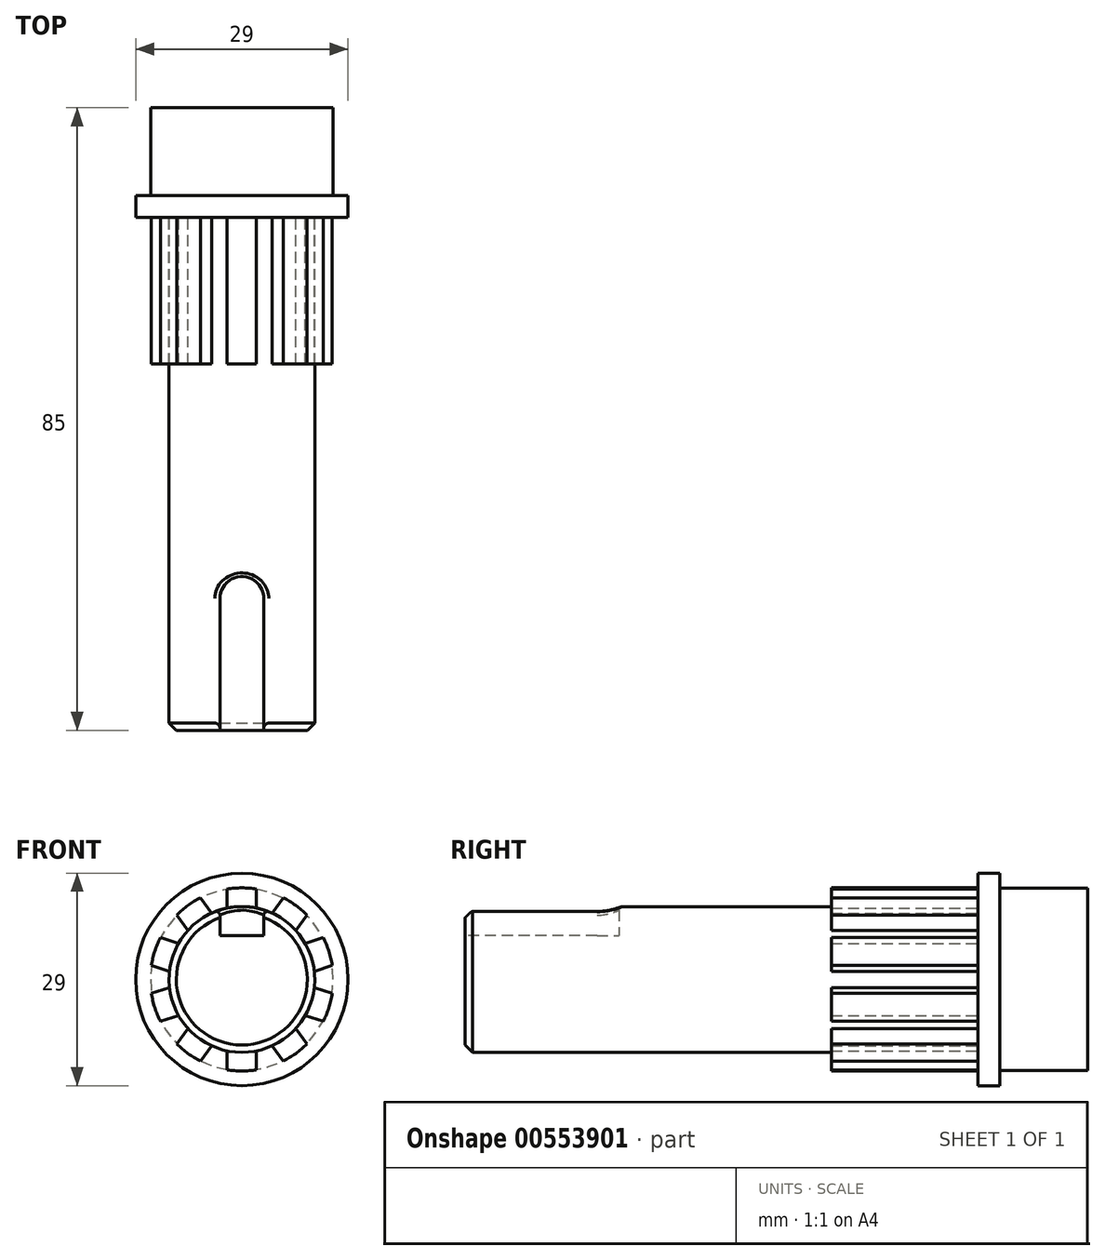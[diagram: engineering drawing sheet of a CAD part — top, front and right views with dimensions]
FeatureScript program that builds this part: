
annotation { "Feature Type Name" : "Feature", "Feature Type Description" : "" }
export const myFeature = defineFeature(function(context is Context, id is Id, definition is map)
    precondition{}
    {
        {
            var Q0;
            Q0=qCreatedBy(makeId("Front.planeOp"),FACE);
            var sketch = newSketch(context, id + "F0", { "sketchPlane" : qUnion([Q0])});
            skCircle(sketch, "E0", {"center": v(0, 0) * mm, "radius": 12.45 * mm});
            skSolve(sketch);
        }
        {
            var Q0;
            Q0=makeQuery(id+"F0.imprint","IMPRINT",FACE,{"disambiguationData":[TD([[makeQuery(id+"F0.imprint","IMPRINT",EDGE,{"derivedFrom":sQuery(id+"F0.wireOp",EDGE,"E0")}),1.0]])]});
            extrude(context, id + "F1", {"entities" : qUnion([Q0]), "oppositeDirection" : true, "depth" : 12 * mm, "offsetDistance" : 25 * mm});
        }
        {
            var Q0;
            Q0=qCreatedBy(makeId("Front.planeOp"),FACE);
            var sketch = newSketch(context, id + "F2", { "sketchPlane" : qUnion([Q0])});
            skCircle(sketch, "E1", {"center": v(0, 0) * mm, "radius": 14.5 * mm});
            skSolve(sketch);
        }
        {
            var Q0;
            Q0=makeQuery(id+"F2.imprint","IMPRINT",FACE,{"disambiguationData":[TD([[makeQuery(id+"F2.imprint","IMPRINT",EDGE,{"derivedFrom":sQuery(id+"F2.wireOp",EDGE,"E1")}),1.0]])]});
            extrude(context, id + "F3", {"entities" : qUnion([Q0]), "operationType" : NewBodyOperationType.ADD, "depth" : 3 * mm, "offsetDistance" : 25 * mm});
        }
        {
            var Q0;
            Q0=makeQuery(id+"F3.opExtrude","CAP_FACE",FACE,{"disambiguationData":[OSD([sQuery(id+"F2.wireOp",EDGE,"E1")])],"isStart":false});
            var sketch = newSketch(context, id + "F4", { "sketchPlane" : qUnion([Q0])});
            skCircle(sketch, "E2", {"center": v(0, 0) * mm, "radius": 9.95 * mm});
            skSolve(sketch);
        }
        {
            var Q0;
            Q0=makeQuery(id+"F4.imprint","IMPRINT",FACE,{"disambiguationData":[TD([[makeQuery(id+"F4.imprint","IMPRINT",EDGE,{"derivedFrom":sQuery(id+"F4.wireOp",EDGE,"E2")}),1.0]])]});
            extrude(context, id + "F5", {"entities" : qUnion([Q0]), "operationType" : NewBodyOperationType.ADD, "depth" : 70 * mm, "offsetDistance" : 25 * mm});
        }
        {
            var Q0;
            Q0=makeQuery(id+"F3.opExtrude","CAP_FACE",FACE,{"disambiguationData":[OSD([sQuery(id+"F2.wireOp",EDGE,"E1")])],"isStart":false});
            var sketch = newSketch(context, id + "F6", { "sketchPlane" : qUnion([Q0])});
            skArc(sketch, "E3", {"start": v(2, 12.34) * mm, "mid": v(0, 12.5) * mm, "end": v(-2, 12.34) * mm});
            skLineSegment(sketch, "E4", {"start": v(-2, 12.34) * mm, "end": v(-2, 8.4) * mm});
            skLineSegment(sketch, "E5", {"start": v(2, 8.4) * mm, "end": v(2, 12.34) * mm});
            skPoint(sketch, "E6.end.orphan", {"position": v(0.2, 8.4) * mm});
            skLineSegment(sketch, "E7.1.0", {"start": v(-8.87, 8.8) * mm, "end": v(-6.56, 5.63) * mm});
            skArc(sketch, "E7.1.1", {"start": v(-5.63, 11.16) * mm, "mid": v(-7.35, 10.11) * mm, "end": v(-8.87, 8.8) * mm});
            skLineSegment(sketch, "E7.1.2", {"start": v(-3.32, 7.98) * mm, "end": v(-5.63, 11.16) * mm});
            skLineSegment(sketch, "E7.2.0", {"start": v(-12.35, 1.91) * mm, "end": v(-8.62, 0.7) * mm});
            skArc(sketch, "E7.2.1", {"start": v(-11.12, 5.72) * mm, "mid": v(-11.89, 3.86) * mm, "end": v(-12.35, 1.91) * mm});
            skLineSegment(sketch, "E7.2.2", {"start": v(-7.38, 4.5) * mm, "end": v(-11.12, 5.72) * mm});
            skLineSegment(sketch, "E7.3.0", {"start": v(-11.12, -5.72) * mm, "end": v(-7.38, -4.5) * mm});
            skArc(sketch, "E7.3.1", {"start": v(-12.35, -1.91) * mm, "mid": v(-11.89, -3.86) * mm, "end": v(-11.12, -5.72) * mm});
            skLineSegment(sketch, "E7.3.2", {"start": v(-8.62, -0.7) * mm, "end": v(-12.35, -1.91) * mm});
            skLineSegment(sketch, "E7.4.0", {"start": v(-5.63, -11.16) * mm, "end": v(-3.32, -7.98) * mm});
            skArc(sketch, "E7.4.1", {"start": v(-8.87, -8.8) * mm, "mid": v(-7.35, -10.11) * mm, "end": v(-5.63, -11.16) * mm});
            skLineSegment(sketch, "E7.4.2", {"start": v(-6.56, -5.63) * mm, "end": v(-8.87, -8.8) * mm});
            skLineSegment(sketch, "E7.5.0", {"start": v(2, -12.34) * mm, "end": v(2, -8.4) * mm});
            skArc(sketch, "E7.5.1", {"start": v(-2, -12.34) * mm, "mid": v(0, -12.5) * mm, "end": v(2, -12.34) * mm});
            skLineSegment(sketch, "E7.5.2", {"start": v(-2, -8.4) * mm, "end": v(-2, -12.34) * mm});
            skLineSegment(sketch, "E7.6.0", {"start": v(8.87, -8.8) * mm, "end": v(6.56, -5.63) * mm});
            skArc(sketch, "E7.6.1", {"start": v(5.63, -11.16) * mm, "mid": v(7.35, -10.11) * mm, "end": v(8.87, -8.8) * mm});
            skLineSegment(sketch, "E7.6.2", {"start": v(3.32, -7.98) * mm, "end": v(5.63, -11.16) * mm});
            skLineSegment(sketch, "E7.7.0", {"start": v(12.35, -1.91) * mm, "end": v(8.62, -0.7) * mm});
            skArc(sketch, "E7.7.1", {"start": v(11.12, -5.72) * mm, "mid": v(11.89, -3.86) * mm, "end": v(12.35, -1.91) * mm});
            skLineSegment(sketch, "E7.7.2", {"start": v(7.38, -4.5) * mm, "end": v(11.12, -5.72) * mm});
            skLineSegment(sketch, "E7.8.0", {"start": v(11.12, 5.72) * mm, "end": v(7.38, 4.5) * mm});
            skArc(sketch, "E7.8.1", {"start": v(12.35, 1.91) * mm, "mid": v(11.89, 3.86) * mm, "end": v(11.12, 5.72) * mm});
            skLineSegment(sketch, "E7.8.2", {"start": v(8.62, 0.7) * mm, "end": v(12.35, 1.91) * mm});
            skLineSegment(sketch, "E7.9.0", {"start": v(5.63, 11.16) * mm, "end": v(3.32, 7.98) * mm});
            skArc(sketch, "E7.9.1", {"start": v(8.87, 8.8) * mm, "mid": v(7.35, 10.11) * mm, "end": v(5.63, 11.16) * mm});
            skLineSegment(sketch, "E7.9.2", {"start": v(6.56, 5.63) * mm, "end": v(8.87, 8.8) * mm});
            skSolve(sketch);
        }
        {
            var Q0;
            {var subQ0=sQuery(id+"F6.wireOp",EDGE,"E3");Q0=makeQuery(id+"F6.imprint","IMPRINT",FACE,{"disambiguationData":[TD([[makeQuery(id+"F6.imprint","IMPRINT",EDGE,{"derivedFrom":subQ0}),1.0]])]});}
            var Q1;
            {var subQ0=sQuery(id+"F6.wireOp",EDGE,"E7.1.1");Q1=makeQuery(id+"F6.imprint","IMPRINT",FACE,{"disambiguationData":[TD([[makeQuery(id+"F6.imprint","IMPRINT",EDGE,{"derivedFrom":subQ0}),1.0]])]});}
            var Q2;
            {var subQ0=sQuery(id+"F6.wireOp",EDGE,"E7.2.1");Q2=makeQuery(id+"F6.imprint","IMPRINT",FACE,{"disambiguationData":[TD([[makeQuery(id+"F6.imprint","IMPRINT",EDGE,{"derivedFrom":subQ0}),1.0]])]});}
            var Q3;
            {var subQ0=sQuery(id+"F6.wireOp",EDGE,"E7.3.1");Q3=makeQuery(id+"F6.imprint","IMPRINT",FACE,{"disambiguationData":[TD([[makeQuery(id+"F6.imprint","IMPRINT",EDGE,{"derivedFrom":subQ0}),1.0]])]});}
            var Q4;
            {var subQ0=sQuery(id+"F6.wireOp",EDGE,"E7.4.1");Q4=makeQuery(id+"F6.imprint","IMPRINT",FACE,{"disambiguationData":[TD([[makeQuery(id+"F6.imprint","IMPRINT",EDGE,{"derivedFrom":subQ0}),1.0]])]});}
            var Q5;
            {var subQ0=sQuery(id+"F6.wireOp",EDGE,"E7.5.1");Q5=makeQuery(id+"F6.imprint","IMPRINT",FACE,{"disambiguationData":[TD([[makeQuery(id+"F6.imprint","IMPRINT",EDGE,{"derivedFrom":subQ0}),1.0]])]});}
            var Q6;
            {var subQ0=sQuery(id+"F6.wireOp",EDGE,"E7.6.1");Q6=makeQuery(id+"F6.imprint","IMPRINT",FACE,{"disambiguationData":[TD([[makeQuery(id+"F6.imprint","IMPRINT",EDGE,{"derivedFrom":subQ0}),1.0]])]});}
            var Q7;
            {var subQ0=sQuery(id+"F6.wireOp",EDGE,"E7.7.1");Q7=makeQuery(id+"F6.imprint","IMPRINT",FACE,{"disambiguationData":[TD([[makeQuery(id+"F6.imprint","IMPRINT",EDGE,{"derivedFrom":subQ0}),1.0]])]});}
            var Q8;
            {var subQ0=sQuery(id+"F6.wireOp",EDGE,"E7.8.1");Q8=makeQuery(id+"F6.imprint","IMPRINT",FACE,{"disambiguationData":[TD([[makeQuery(id+"F6.imprint","IMPRINT",EDGE,{"derivedFrom":subQ0}),1.0]])]});}
            var Q9;
            {var subQ0=sQuery(id+"F6.wireOp",EDGE,"E7.9.1");Q9=makeQuery(id+"F6.imprint","IMPRINT",FACE,{"disambiguationData":[TD([[makeQuery(id+"F6.imprint","IMPRINT",EDGE,{"derivedFrom":subQ0}),1.0]])]});}
            extrude(context, id + "F7", {"entities" : qUnion([Q0, Q1, Q2, Q3, Q4, Q5, Q6, Q7, Q8, Q9]), "operationType" : NewBodyOperationType.ADD, "depth" : 20 * mm, "offsetDistance" : 25 * mm});
        }
        {
            var Q0;
            Q0=qCreatedBy(makeId("Top.planeOp"),FACE);
            cPlane(context, id + "F8", {"entities" : qUnion([Q0]), "cplaneType" : CPlaneType.OFFSET, "offset" : 6 * mm, "width" : 150 * mm, "height" : 150 * mm});
        }
        {
            var Q0;
            Q0=qCreatedBy(id+"F8.planeOp",FACE);
            var sketch = newSketch(context, id + "F9", { "sketchPlane" : qUnion([Q0])});
            skLineSegment(sketch, "E8.top", {"start": v(-3, -85) * mm, "end": v(3, -85) * mm});
            skLineSegment(sketch, "E8.left", {"start": v(-3, -55) * mm, "end": v(-3, -85) * mm});
            skLineSegment(sketch, "E8.right", {"start": v(3, -55) * mm, "end": v(3, -85) * mm});
            skArc(sketch, "E9", {"start": v(3, -55) * mm, "mid": v(0, -52) * mm, "end": v(-3, -55) * mm});
            skSolve(sketch);
        }
        {
            var Q0;
            Q0 = qSketchRegion(id + "F9", true);
            extrude(context, id + "F10", {"entities" : qUnion([Q0]), "operationType" : NewBodyOperationType.REMOVE, "depth" : 10 * mm, "offsetDistance" : 25 * mm});
        }
        {
            var Q0;
            Q0=makeQuery(id+"F5.opExtrude","CAP_EDGE",EDGE,{"disambiguationData":[OSD([sQuery(id+"F4.wireOp",EDGE,"E2")])],"isStart":false});
            chamfer(context, id + "F11", {"entities" : qUnion([Q0]), "width" : 1 * mm, "tangentPropagation" : true});
        }
        {
            var Q0;
            Q0=makeQuery(id+"F10.boolean.opBoolean","INTERSECT",EDGE,{"derivedFrom":[makeQuery(id+"F5.opExtrude","SWEPT_FACE",FACE,{"disambiguationData":[OSD([sQuery(id+"F4.wireOp",EDGE,"E2")])]}),makeQuery(id+"F10.opExtrude","SWEPT_FACE",FACE,{"disambiguationData":[OSD([sQuery(id+"F9.wireOp",EDGE,"E8.left")])]})]});
            var Q1;
            Q1=makeQuery(id+"F10.boolean.opBoolean","INTERSECT",EDGE,{"derivedFrom":[makeQuery(id+"F5.opExtrude","SWEPT_FACE",FACE,{"disambiguationData":[OSD([sQuery(id+"F4.wireOp",EDGE,"E2")])]}),makeQuery(id+"F10.opExtrude","SWEPT_FACE",FACE,{"disambiguationData":[OSD([sQuery(id+"F9.wireOp",EDGE,"E9")])]})]});
            var Q2;
            Q2=makeQuery(id+"F10.boolean.opBoolean","INTERSECT",EDGE,{"derivedFrom":[makeQuery(id+"F5.opExtrude","SWEPT_FACE",FACE,{"disambiguationData":[OSD([sQuery(id+"F4.wireOp",EDGE,"E2")])]}),makeQuery(id+"F10.opExtrude","SWEPT_FACE",FACE,{"disambiguationData":[OSD([sQuery(id+"F9.wireOp",EDGE,"E8.right")])]})]});
            fillet(context, id + "F12", {"entities" : qUnion([Q0, Q1, Q2]), "radius" : .5 * mm, "tangentPropagation" : true, "allowEdgeOverflow" : false});
        }
    });
